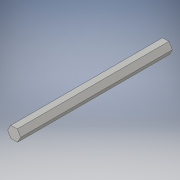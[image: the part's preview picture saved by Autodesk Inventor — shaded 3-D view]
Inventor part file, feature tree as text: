
AUTODESK INVENTOR PART (.ipt)
format: ipt  version: 2016 (Build 200138000, 138)  size: 90,112 bytes
history: native  units: in
note: dims shown in document units (in); Inventor stores cm internally (conversion verified against a paired STEP export)
features: extrude x1, sketch x1
ambient origin geometry x8: Origin, YZ Plane, XZ Plane, XY Plane, X Axis, Y Axis, Z Axis, Center Point
bodies: Solid1 (feature_tree)
feature tree (2):
  extrude  "Extrusion1"  Depth=6.675in TaperAngle=0.0deg
  sketch  "Sketch1"  dims[d0=0.5in d1=6.675in d2=0.0in]
